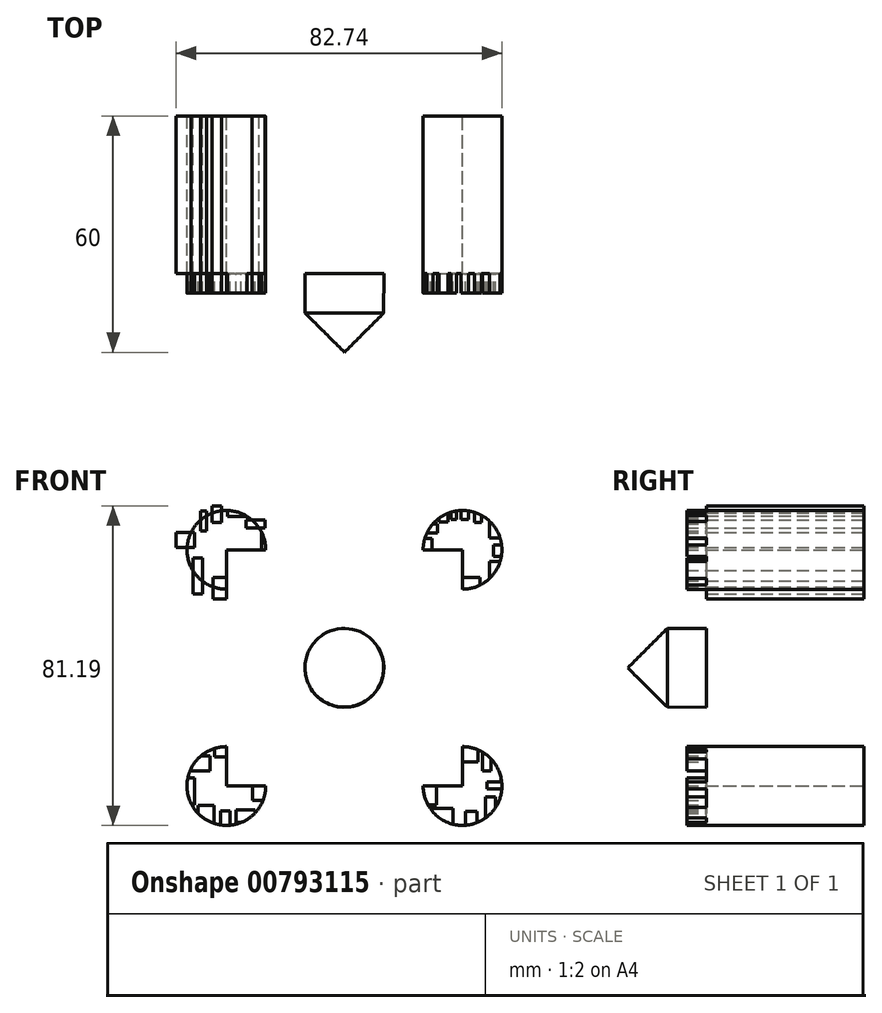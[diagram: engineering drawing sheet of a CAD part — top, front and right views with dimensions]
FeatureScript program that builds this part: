
annotation { "Feature Type Name" : "Feature", "Feature Type Description" : "" }
export const myFeature = defineFeature(function(context is Context, id is Id, definition is map)
    precondition{}
    {
        {
            var Q0;
            Q0=qCreatedBy(makeId("Front.planeOp"),FACE);
            var sketch = newSketch(context, id + "F0", { "sketchPlane" : qUnion([Q0])});
            skLineSegment(sketch, "E0.top", {"start": v(-31.3, 38.66) * mm, "end": v(28.7, 38.66) * mm});
            skLineSegment(sketch, "E0.right", {"start": v(28.7, -21.34) * mm, "end": v(28.7, 38.66) * mm});
            skCircle(sketch, "E1", {"center": v(-31.3, 38.66) * mm, "radius": 10 * mm});
            skCircle(sketch, "E2", {"center": v(28.7, 38.66) * mm, "radius": 10 * mm});
            skCircle(sketch, "E3", {"center": v(-31.3, -21.34) * mm, "radius": 10 * mm});
            skLineSegment(sketch, "E4", {"start": v(28.7, -21.34) * mm, "end": v(-31.3, -21.34) * mm});
            skLineSegment(sketch, "E5", {"start": v(-31.3, 38.66) * mm, "end": v(-31.3, -21.34) * mm});
            skLineSegment(sketch, "E6.bottom", {"start": v(-31.3, 26.14) * mm, "end": v(-34.66, 26.14) * mm});
            skLineSegment(sketch, "E6.top", {"start": v(-31.3, 31.59) * mm, "end": v(-34.66, 31.59) * mm});
            skLineSegment(sketch, "E6.left", {"start": v(-31.3, 26.14) * mm, "end": v(-31.3, 31.59) * mm});
            skLineSegment(sketch, "E6.right", {"start": v(-34.66, 26.14) * mm, "end": v(-34.66, 31.59) * mm});
            skLineSegment(sketch, "E7.bottom", {"start": v(-37.36, 27.46) * mm, "end": v(-39.78, 27.46) * mm});
            skLineSegment(sketch, "E7.top", {"start": v(-37.36, 36.62) * mm, "end": v(-39.78, 36.62) * mm});
            skLineSegment(sketch, "E7.left", {"start": v(-37.36, 27.46) * mm, "end": v(-37.36, 36.62) * mm});
            skLineSegment(sketch, "E7.right", {"start": v(-39.78, 27.46) * mm, "end": v(-39.78, 36.62) * mm});
            skLineSegment(sketch, "E8.bottom", {"start": v(-19.52, 38.66) * mm, "end": v(-22.4, 38.66) * mm});
            skLineSegment(sketch, "E8.top", {"start": v(-19.52, 43.23) * mm, "end": v(-22.4, 43.23) * mm});
            skLineSegment(sketch, "E8.left", {"start": v(-19.52, 38.66) * mm, "end": v(-19.52, 43.23) * mm});
            skLineSegment(sketch, "E8.right", {"start": v(-22.4, 38.66) * mm, "end": v(-22.4, 43.23) * mm});
            skLineSegment(sketch, "E9.bottom", {"start": v(-21.44, 46.19) * mm, "end": v(-26.35, 46.19) * mm});
            skLineSegment(sketch, "E9.top", {"start": v(-21.44, 44.24) * mm, "end": v(-26.35, 44.24) * mm});
            skLineSegment(sketch, "E9.left", {"start": v(-21.44, 46.19) * mm, "end": v(-21.44, 44.24) * mm});
            skLineSegment(sketch, "E9.right", {"start": v(-26.35, 46.19) * mm, "end": v(-26.35, 44.24) * mm});
            skLineSegment(sketch, "E10.bottom", {"start": v(-25.81, 49.08) * mm, "end": v(-30.99, 49.08) * mm});
            skLineSegment(sketch, "E10.top", {"start": v(-25.81, 47.12) * mm, "end": v(-30.99, 47.12) * mm});
            skLineSegment(sketch, "E10.left", {"start": v(-25.81, 49.08) * mm, "end": v(-25.81, 47.12) * mm});
            skLineSegment(sketch, "E10.right", {"start": v(-30.99, 49.08) * mm, "end": v(-30.99, 47.12) * mm});
            skLineSegment(sketch, "E11.bottom", {"start": v(-32.51, 49.85) * mm, "end": v(-34.9, 49.85) * mm});
            skLineSegment(sketch, "E11.top", {"start": v(-32.51, 45.58) * mm, "end": v(-34.9, 45.58) * mm});
            skLineSegment(sketch, "E11.left", {"start": v(-32.51, 49.85) * mm, "end": v(-32.51, 45.58) * mm});
            skLineSegment(sketch, "E11.right", {"start": v(-34.9, 49.85) * mm, "end": v(-34.9, 45.58) * mm});
            skLineSegment(sketch, "E12.bottom", {"start": v(-37.8, 48.54) * mm, "end": v(-36.34, 48.54) * mm});
            skLineSegment(sketch, "E12.top", {"start": v(-37.8, 43.44) * mm, "end": v(-36.34, 43.44) * mm});
            skLineSegment(sketch, "E12.left", {"start": v(-37.8, 48.54) * mm, "end": v(-37.8, 43.44) * mm});
            skLineSegment(sketch, "E12.right", {"start": v(-36.34, 48.54) * mm, "end": v(-36.34, 43.44) * mm});
            skLineSegment(sketch, "E13.bottom", {"start": v(-44.04, 43.08) * mm, "end": v(-39.35, 43.08) * mm});
            skLineSegment(sketch, "E13.top", {"start": v(-44.04, 39.2) * mm, "end": v(-39.35, 39.2) * mm});
            skLineSegment(sketch, "E13.left", {"start": v(-44.04, 43.08) * mm, "end": v(-44.04, 39.2) * mm});
            skLineSegment(sketch, "E13.right", {"start": v(-39.35, 43.08) * mm, "end": v(-39.35, 39.2) * mm});
            skLineSegment(sketch, "E14.bottom", {"start": v(17.29, 38.66) * mm, "end": v(20.94, 38.66) * mm});
            skLineSegment(sketch, "E14.top", {"start": v(17.29, 41.51) * mm, "end": v(20.94, 41.51) * mm});
            skLineSegment(sketch, "E14.left", {"start": v(17.29, 38.66) * mm, "end": v(17.29, 41.51) * mm});
            skLineSegment(sketch, "E14.right", {"start": v(20.94, 38.66) * mm, "end": v(20.94, 41.51) * mm});
            skLineSegment(sketch, "E15.bottom", {"start": v(19, 42.93) * mm, "end": v(22.3, 42.93) * mm});
            skLineSegment(sketch, "E15.top", {"start": v(19, 45.24) * mm, "end": v(22.3, 45.24) * mm});
            skLineSegment(sketch, "E15.left", {"start": v(19, 42.93) * mm, "end": v(19, 45.24) * mm});
            skLineSegment(sketch, "E15.right", {"start": v(22.3, 42.93) * mm, "end": v(22.3, 45.24) * mm});
            skLineSegment(sketch, "E16.bottom", {"start": v(22.73, 48.54) * mm, "end": v(25, 48.54) * mm});
            skLineSegment(sketch, "E16.top", {"start": v(22.73, 45.75) * mm, "end": v(25, 45.75) * mm});
            skLineSegment(sketch, "E16.left", {"start": v(22.73, 48.54) * mm, "end": v(22.73, 45.75) * mm});
            skLineSegment(sketch, "E16.right", {"start": v(25, 48.54) * mm, "end": v(25, 45.75) * mm});
            skLineSegment(sketch, "E17.bottom", {"start": v(27.22, 48.99) * mm, "end": v(25.81, 48.99) * mm});
            skLineSegment(sketch, "E17.top", {"start": v(27.22, 46.33) * mm, "end": v(25.81, 46.33) * mm});
            skLineSegment(sketch, "E17.left", {"start": v(27.22, 48.99) * mm, "end": v(27.22, 46.33) * mm});
            skLineSegment(sketch, "E17.right", {"start": v(25.81, 48.99) * mm, "end": v(25.81, 46.33) * mm});
            skLineSegment(sketch, "E18.bottom", {"start": v(28.32, 49.76) * mm, "end": v(30.22, 49.76) * mm});
            skLineSegment(sketch, "E18.top", {"start": v(28.32, 46.32) * mm, "end": v(30.22, 46.32) * mm});
            skLineSegment(sketch, "E18.left", {"start": v(28.32, 49.76) * mm, "end": v(28.32, 46.32) * mm});
            skLineSegment(sketch, "E18.right", {"start": v(30.22, 49.76) * mm, "end": v(30.22, 46.32) * mm});
            skLineSegment(sketch, "E19.bottom", {"start": v(31.72, 49.12) * mm, "end": v(33.5, 49.12) * mm});
            skLineSegment(sketch, "E19.top", {"start": v(31.72, 45.6) * mm, "end": v(33.5, 45.6) * mm});
            skLineSegment(sketch, "E19.left", {"start": v(31.72, 49.12) * mm, "end": v(31.72, 45.6) * mm});
            skLineSegment(sketch, "E19.right", {"start": v(33.5, 49.12) * mm, "end": v(33.5, 45.6) * mm});
            skCircle(sketch, "E20", {"center": v(28.7, -21.34) * mm, "radius": 10 * mm});
            skLineSegment(sketch, "E21.bottom", {"start": v(28.7, 26.02) * mm, "end": v(33.17, 26.02) * mm});
            skLineSegment(sketch, "E21.top", {"start": v(28.7, 31.7) * mm, "end": v(33.17, 31.7) * mm});
            skLineSegment(sketch, "E21.left", {"start": v(28.7, 26.02) * mm, "end": v(28.7, 31.7) * mm});
            skLineSegment(sketch, "E21.right", {"start": v(33.17, 26.02) * mm, "end": v(33.17, 31.7) * mm});
            skLineSegment(sketch, "E22.bottom", {"start": v(35.6, 29.26) * mm, "end": v(38.26, 29.26) * mm});
            skLineSegment(sketch, "E22.top", {"start": v(35.6, 35.7) * mm, "end": v(38.26, 35.7) * mm});
            skLineSegment(sketch, "E22.left", {"start": v(35.6, 29.26) * mm, "end": v(35.6, 35.7) * mm});
            skLineSegment(sketch, "E22.right", {"start": v(38.26, 29.26) * mm, "end": v(38.26, 35.7) * mm});
            skLineSegment(sketch, "E23.bottom", {"start": v(35.6, 48.4) * mm, "end": v(38.24, 48.4) * mm});
            skLineSegment(sketch, "E23.top", {"start": v(35.6, 41.64) * mm, "end": v(38.24, 41.64) * mm});
            skLineSegment(sketch, "E23.left", {"start": v(35.6, 48.4) * mm, "end": v(35.6, 41.64) * mm});
            skLineSegment(sketch, "E23.right", {"start": v(38.24, 48.4) * mm, "end": v(38.24, 41.64) * mm});
            skLineSegment(sketch, "E24.bottom", {"start": v(40.87, 36.96) * mm, "end": v(36.52, 36.96) * mm});
            skLineSegment(sketch, "E24.top", {"start": v(40.87, 39.9) * mm, "end": v(36.52, 39.9) * mm});
            skLineSegment(sketch, "E24.left", {"start": v(40.87, 36.96) * mm, "end": v(40.87, 39.9) * mm});
            skLineSegment(sketch, "E24.right", {"start": v(36.52, 36.96) * mm, "end": v(36.52, 39.9) * mm});
            skLineSegment(sketch, "E25.bottom", {"start": v(28.7, -8.22) * mm, "end": v(32.65, -8.22) * mm});
            skLineSegment(sketch, "E25.top", {"start": v(28.7, -15.2) * mm, "end": v(32.65, -15.2) * mm});
            skLineSegment(sketch, "E25.left", {"start": v(28.7, -8.22) * mm, "end": v(28.7, -15.2) * mm});
            skLineSegment(sketch, "E25.right", {"start": v(32.65, -8.22) * mm, "end": v(32.65, -15.2) * mm});
            skLineSegment(sketch, "E26.bottom", {"start": v(35.9, -10.63) * mm, "end": v(33.73, -10.63) * mm});
            skLineSegment(sketch, "E26.top", {"start": v(35.9, -17.5) * mm, "end": v(33.73, -17.5) * mm});
            skLineSegment(sketch, "E26.left", {"start": v(35.9, -10.63) * mm, "end": v(35.9, -17.5) * mm});
            skLineSegment(sketch, "E26.right", {"start": v(33.73, -10.63) * mm, "end": v(33.73, -17.5) * mm});
            skLineSegment(sketch, "E27.bottom", {"start": v(15.4, -21.34) * mm, "end": v(22.15, -21.34) * mm});
            skLineSegment(sketch, "E27.top", {"start": v(15.4, -26.11) * mm, "end": v(22.15, -26.11) * mm});
            skLineSegment(sketch, "E27.left", {"start": v(15.4, -21.34) * mm, "end": v(15.4, -26.11) * mm});
            skLineSegment(sketch, "E27.right", {"start": v(22.15, -21.34) * mm, "end": v(22.15, -26.11) * mm});
            skLineSegment(sketch, "E28.bottom", {"start": v(19.62, -31.77) * mm, "end": v(26.25, -31.77) * mm});
            skLineSegment(sketch, "E28.top", {"start": v(19.62, -27.07) * mm, "end": v(26.25, -27.07) * mm});
            skLineSegment(sketch, "E28.left", {"start": v(19.62, -31.77) * mm, "end": v(19.62, -27.07) * mm});
            skLineSegment(sketch, "E28.right", {"start": v(26.25, -31.77) * mm, "end": v(26.25, -27.07) * mm});
            skLineSegment(sketch, "E29.bottom", {"start": v(29.5, -34.42) * mm, "end": v(32.39, -34.42) * mm});
            skLineSegment(sketch, "E29.top", {"start": v(29.5, -27.8) * mm, "end": v(32.39, -27.8) * mm});
            skLineSegment(sketch, "E29.left", {"start": v(29.5, -34.42) * mm, "end": v(29.5, -27.8) * mm});
            skLineSegment(sketch, "E29.right", {"start": v(32.39, -34.42) * mm, "end": v(32.39, -27.8) * mm});
            skLineSegment(sketch, "E30.bottom", {"start": v(37.08, -29.48) * mm, "end": v(34.56, -29.48) * mm});
            skLineSegment(sketch, "E30.top", {"start": v(37.08, -24.06) * mm, "end": v(34.56, -24.06) * mm});
            skLineSegment(sketch, "E30.left", {"start": v(37.08, -29.48) * mm, "end": v(37.08, -24.06) * mm});
            skLineSegment(sketch, "E30.right", {"start": v(34.56, -29.48) * mm, "end": v(34.56, -24.06) * mm});
            skLineSegment(sketch, "E31.bottom", {"start": v(41.06, -20.33) * mm, "end": v(34.92, -20.33) * mm});
            skLineSegment(sketch, "E31.top", {"start": v(41.06, -22.14) * mm, "end": v(34.92, -22.14) * mm});
            skLineSegment(sketch, "E31.left", {"start": v(41.06, -20.33) * mm, "end": v(41.06, -22.14) * mm});
            skLineSegment(sketch, "E31.right", {"start": v(34.92, -20.33) * mm, "end": v(34.92, -22.14) * mm});
            skLineSegment(sketch, "E32.bottom", {"start": v(-18.04, -21.34) * mm, "end": v(-24.67, -21.34) * mm});
            skLineSegment(sketch, "E32.top", {"start": v(-18.04, -24.96) * mm, "end": v(-24.67, -24.96) * mm});
            skLineSegment(sketch, "E32.left", {"start": v(-18.04, -21.34) * mm, "end": v(-18.04, -24.96) * mm});
            skLineSegment(sketch, "E32.right", {"start": v(-24.67, -21.34) * mm, "end": v(-24.67, -24.96) * mm});
            skLineSegment(sketch, "E33.bottom", {"start": v(-24.07, -30.62) * mm, "end": v(-28.88, -30.62) * mm});
            skLineSegment(sketch, "E33.top", {"start": v(-24.07, -27.37) * mm, "end": v(-28.88, -27.37) * mm});
            skLineSegment(sketch, "E33.left", {"start": v(-24.07, -30.62) * mm, "end": v(-24.07, -27.37) * mm});
            skLineSegment(sketch, "E33.right", {"start": v(-28.88, -30.62) * mm, "end": v(-28.88, -27.37) * mm});
            skLineSegment(sketch, "E34.bottom", {"start": v(-32.74, -33.39) * mm, "end": v(-30.33, -33.39) * mm});
            skLineSegment(sketch, "E34.top", {"start": v(-32.74, -27.6) * mm, "end": v(-30.33, -27.6) * mm});
            skLineSegment(sketch, "E34.left", {"start": v(-32.74, -33.39) * mm, "end": v(-32.74, -27.6) * mm});
            skLineSegment(sketch, "E34.right", {"start": v(-30.33, -33.39) * mm, "end": v(-30.33, -27.6) * mm});
            skLineSegment(sketch, "E35.bottom", {"start": v(-38.52, -31.1) * mm, "end": v(-34.42, -31.1) * mm});
            skLineSegment(sketch, "E35.top", {"start": v(-38.52, -26.28) * mm, "end": v(-34.42, -26.28) * mm});
            skLineSegment(sketch, "E35.left", {"start": v(-38.52, -31.1) * mm, "end": v(-38.52, -26.28) * mm});
            skLineSegment(sketch, "E35.right", {"start": v(-34.42, -31.1) * mm, "end": v(-34.42, -26.28) * mm});
            skLineSegment(sketch, "E36.bottom", {"start": v(-42.85, -26.16) * mm, "end": v(-39.36, -26.16) * mm});
            skLineSegment(sketch, "E36.top", {"start": v(-42.85, -19.3) * mm, "end": v(-39.36, -19.3) * mm});
            skLineSegment(sketch, "E36.left", {"start": v(-42.85, -26.16) * mm, "end": v(-42.85, -19.3) * mm});
            skLineSegment(sketch, "E36.right", {"start": v(-39.36, -26.16) * mm, "end": v(-39.36, -19.3) * mm});
            skLineSegment(sketch, "E37.bottom", {"start": v(-41.9, -13.64) * mm, "end": v(-35.39, -13.64) * mm});
            skLineSegment(sketch, "E37.top", {"start": v(-41.9, -17.5) * mm, "end": v(-35.39, -17.5) * mm});
            skLineSegment(sketch, "E37.left", {"start": v(-41.9, -13.64) * mm, "end": v(-41.9, -17.5) * mm});
            skLineSegment(sketch, "E37.right", {"start": v(-35.39, -13.64) * mm, "end": v(-35.39, -17.5) * mm});
            skLineSegment(sketch, "E38.bottom", {"start": v(-31.3, -7.86) * mm, "end": v(-34.3, -7.86) * mm});
            skLineSegment(sketch, "E38.top", {"start": v(-31.3, -14) * mm, "end": v(-34.3, -14) * mm});
            skLineSegment(sketch, "E38.left", {"start": v(-31.3, -7.86) * mm, "end": v(-31.3, -14) * mm});
            skLineSegment(sketch, "E38.right", {"start": v(-34.3, -7.86) * mm, "end": v(-34.3, -14) * mm});
            skSolve(sketch);
        }
        {
            var Q0;
            {var subQ0=sQuery(id+"F0.wireOp",EDGE,"E8.bottom");var subQ3=sQuery(id+"F0.wireOp",EDGE,"E1");var subQ4=makeQuery(id+"F0.imprint","INTERSECT",VERTEX,{"derivedFrom":[subQ3,subQ0]});Q0=makeQuery(id+"F0.imprint","IMPRINT",FACE,{"disambiguationData":[TD([[makeQuery(id+"F0.imprint","IMPRINT",EDGE,{"disambiguationData":[TD([[subQ4,1.0]])],"derivedFrom":subQ3}),-1.0]])]});}
            var Q1;
            {var subQ3=sQuery(id+"F0.wireOp",EDGE,"E3");var subQ7=sQuery(id+"F0.wireOp",EDGE,"E38.left");var subQ9=makeQuery(id+"F0.imprint","INTERSECT",VERTEX,{"derivedFrom":[subQ3,subQ7]});Q1=makeQuery(id+"F0.imprint","IMPRINT",FACE,{"disambiguationData":[TD([[makeQuery(id+"F0.imprint","IMPRINT",EDGE,{"disambiguationData":[TD([[subQ9,1.0]])],"derivedFrom":subQ3}),1.0]])]});}
            var Q2;
            {var subQ0=sQuery(id+"F0.wireOp",EDGE,"E25.left");var subQ3=sQuery(id+"F0.wireOp",EDGE,"E20");var subQ4=makeQuery(id+"F0.imprint","INTERSECT",VERTEX,{"derivedFrom":[subQ3,subQ0]});Q2=makeQuery(id+"F0.imprint","IMPRINT",FACE,{"disambiguationData":[TD([[makeQuery(id+"F0.imprint","IMPRINT",EDGE,{"disambiguationData":[TD([[subQ4,-1.0]])],"derivedFrom":subQ3}),1.0]])]});}
            var Q3;
            {var subQ0=sQuery(id+"F0.wireOp",EDGE,"E14.bottom");var subQ1=sQuery(id+"F0.wireOp",EDGE,"E2");var subQ2=makeQuery(id+"F0.imprint","INTERSECT",VERTEX,{"derivedFrom":[subQ1,subQ0]});Q3=makeQuery(id+"F0.imprint","IMPRINT",FACE,{"disambiguationData":[TD([[makeQuery(id+"F0.imprint","IMPRINT",EDGE,{"disambiguationData":[TD([[subQ2,-1.0]])],"derivedFrom":subQ1}),1.0]])]});}
            var Q4;
            {var subQ5=sQuery(id+"F0.wireOp",EDGE,"E8.bottom");var subQ6=sQuery(id+"F0.wireOp",EDGE,"E1");var subQ7=makeQuery(id+"F0.imprint","INTERSECT",VERTEX,{"derivedFrom":[subQ6,subQ5]});Q4=makeQuery(id+"F0.imprint","IMPRINT",FACE,{"disambiguationData":[TD([[makeQuery(id+"F0.imprint","IMPRINT",EDGE,{"disambiguationData":[TD([[subQ7,1.0]])],"derivedFrom":subQ6}),1.0]])]});}
            var Q5;
            {var subQ19=sQuery(id+"F0.wireOp",EDGE,"E6.top");Q5=makeQuery(id+"F0.imprint","IMPRINT",FACE,{"disambiguationData":[TD([[makeQuery(id+"F0.imprint","IMPRINT",EDGE,{"derivedFrom":subQ19}),-1.0]])]});}
            var Q6;
            {var subQ6=sQuery(id+"F0.wireOp",EDGE,"E14.right");Q6=makeQuery(id+"F0.imprint","IMPRINT",FACE,{"disambiguationData":[TD([[makeQuery(id+"F0.imprint","IMPRINT",EDGE,{"derivedFrom":subQ6}),-1.0]])]});}
            var Q7;
            {var subQ12=sQuery(id+"F0.wireOp",EDGE,"E32.right");Q7=makeQuery(id+"F0.imprint","IMPRINT",FACE,{"disambiguationData":[TD([[makeQuery(id+"F0.imprint","IMPRINT",EDGE,{"derivedFrom":subQ12}),-1.0]])]});}
            var Q8;
            {var subQ33=sQuery(id+"F0.wireOp",EDGE,"E25.top");Q8=makeQuery(id+"F0.imprint","IMPRINT",FACE,{"disambiguationData":[TD([[makeQuery(id+"F0.imprint","IMPRINT",EDGE,{"derivedFrom":subQ33}),-1.0]])]});}
            extrude(context, id + "F1", {"entities" : qUnion([Q0, Q1, Q2, Q3, Q4, Q5, Q6, Q7, Q8]), "depth" : 40 * mm, "offsetDistance" : 25 * mm});
        }
        {
            var Q0;
            {var subQ0=sQuery(id+"F0.wireOp",EDGE,"E8.right");Q0=makeQuery(id+"F0.imprint","IMPRINT",FACE,{"disambiguationData":[TD([[makeQuery(id+"F0.imprint","IMPRINT",EDGE,{"derivedFrom":subQ0}),-1.0]])]});}
            var Q1;
            {var subQ5=sQuery(id+"F0.wireOp",EDGE,"E9.right");Q1=makeQuery(id+"F0.imprint","IMPRINT",FACE,{"disambiguationData":[TD([[makeQuery(id+"F0.imprint","IMPRINT",EDGE,{"derivedFrom":subQ5}),1.0]])]});}
            var Q2;
            {var subQ0=sQuery(id+"F0.wireOp",EDGE,"E10.top");var subQ1=sQuery(id+"F0.wireOp",EDGE,"E1");var subQ2=makeQuery(id+"F0.imprint","INTERSECT",VERTEX,{"derivedFrom":[subQ1,subQ0]});Q2=makeQuery(id+"F0.imprint","IMPRINT",FACE,{"disambiguationData":[TD([[makeQuery(id+"F0.imprint","IMPRINT",EDGE,{"disambiguationData":[TD([[subQ2,-1.0]])],"derivedFrom":subQ1}),1.0]])]});}
            var Q3;
            {var subQ5=sQuery(id+"F0.wireOp",EDGE,"E11.top");Q3=makeQuery(id+"F0.imprint","IMPRINT",FACE,{"disambiguationData":[TD([[makeQuery(id+"F0.imprint","IMPRINT",EDGE,{"derivedFrom":subQ5}),-1.0]])]});}
            var Q4;
            {var subQ5=sQuery(id+"F0.wireOp",EDGE,"E12.top");Q4=makeQuery(id+"F0.imprint","IMPRINT",FACE,{"disambiguationData":[TD([[makeQuery(id+"F0.imprint","IMPRINT",EDGE,{"derivedFrom":subQ5}),1.0]])]});}
            var Q5;
            {var subQ5=sQuery(id+"F0.wireOp",EDGE,"E13.right");Q5=makeQuery(id+"F0.imprint","IMPRINT",FACE,{"disambiguationData":[TD([[makeQuery(id+"F0.imprint","IMPRINT",EDGE,{"derivedFrom":subQ5}),-1.0]])]});}
            var Q6;
            {var subQ5=sQuery(id+"F0.wireOp",EDGE,"E7.top");Q6=makeQuery(id+"F0.imprint","IMPRINT",FACE,{"disambiguationData":[TD([[makeQuery(id+"F0.imprint","IMPRINT",EDGE,{"derivedFrom":subQ5}),1.0]])]});}
            var Q7;
            {var subQ5=sQuery(id+"F0.wireOp",EDGE,"E6.top");Q7=makeQuery(id+"F0.imprint","IMPRINT",FACE,{"disambiguationData":[TD([[makeQuery(id+"F0.imprint","IMPRINT",EDGE,{"derivedFrom":subQ5}),1.0]])]});}
            var Q8;
            {var subQ5=sQuery(id+"F0.wireOp",EDGE,"E38.top");Q8=makeQuery(id+"F0.imprint","IMPRINT",FACE,{"disambiguationData":[TD([[makeQuery(id+"F0.imprint","IMPRINT",EDGE,{"derivedFrom":subQ5}),-1.0]])]});}
            var Q9;
            {var subQ5=sQuery(id+"F0.wireOp",EDGE,"E37.right");Q9=makeQuery(id+"F0.imprint","IMPRINT",FACE,{"disambiguationData":[TD([[makeQuery(id+"F0.imprint","IMPRINT",EDGE,{"derivedFrom":subQ5}),-1.0]])]});}
            var Q10;
            {var subQ5=sQuery(id+"F0.wireOp",EDGE,"E36.right");Q10=makeQuery(id+"F0.imprint","IMPRINT",FACE,{"disambiguationData":[TD([[makeQuery(id+"F0.imprint","IMPRINT",EDGE,{"derivedFrom":subQ5}),1.0]])]});}
            var Q11;
            {var subQ5=sQuery(id+"F0.wireOp",EDGE,"E35.top");Q11=makeQuery(id+"F0.imprint","IMPRINT",FACE,{"disambiguationData":[TD([[makeQuery(id+"F0.imprint","IMPRINT",EDGE,{"derivedFrom":subQ5}),-1.0]])]});}
            var Q12;
            {var subQ5=sQuery(id+"F0.wireOp",EDGE,"E34.top");Q12=makeQuery(id+"F0.imprint","IMPRINT",FACE,{"disambiguationData":[TD([[makeQuery(id+"F0.imprint","IMPRINT",EDGE,{"derivedFrom":subQ5}),-1.0]])]});}
            var Q13;
            {var subQ0=sQuery(id+"F0.wireOp",EDGE,"E33.top");Q13=makeQuery(id+"F0.imprint","IMPRINT",FACE,{"disambiguationData":[TD([[makeQuery(id+"F0.imprint","IMPRINT",EDGE,{"derivedFrom":subQ0}),1.0]])]});}
            var Q14;
            {var subQ5=sQuery(id+"F0.wireOp",EDGE,"E32.right");Q14=makeQuery(id+"F0.imprint","IMPRINT",FACE,{"disambiguationData":[TD([[makeQuery(id+"F0.imprint","IMPRINT",EDGE,{"derivedFrom":subQ5}),1.0]])]});}
            var Q15;
            {var subQ5=sQuery(id+"F0.wireOp",EDGE,"E27.right");Q15=makeQuery(id+"F0.imprint","IMPRINT",FACE,{"disambiguationData":[TD([[makeQuery(id+"F0.imprint","IMPRINT",EDGE,{"derivedFrom":subQ5}),-1.0]])]});}
            var Q16;
            {var subQ0=sQuery(id+"F0.wireOp",EDGE,"E28.top");var subQ1=sQuery(id+"F0.wireOp",EDGE,"E20");var subQ2=makeQuery(id+"F0.imprint","INTERSECT",VERTEX,{"derivedFrom":[subQ1,subQ0]});Q16=makeQuery(id+"F0.imprint","IMPRINT",FACE,{"disambiguationData":[TD([[makeQuery(id+"F0.imprint","IMPRINT",EDGE,{"disambiguationData":[TD([[subQ2,-1.0]])],"derivedFrom":subQ1}),1.0]])]});}
            var Q17;
            {var subQ5=sQuery(id+"F0.wireOp",EDGE,"E29.top");Q17=makeQuery(id+"F0.imprint","IMPRINT",FACE,{"disambiguationData":[TD([[makeQuery(id+"F0.imprint","IMPRINT",EDGE,{"derivedFrom":subQ5}),-1.0]])]});}
            var Q18;
            {var subQ5=sQuery(id+"F0.wireOp",EDGE,"E30.top");Q18=makeQuery(id+"F0.imprint","IMPRINT",FACE,{"disambiguationData":[TD([[makeQuery(id+"F0.imprint","IMPRINT",EDGE,{"derivedFrom":subQ5}),1.0]])]});}
            var Q19;
            {var subQ5=sQuery(id+"F0.wireOp",EDGE,"E31.right");Q19=makeQuery(id+"F0.imprint","IMPRINT",FACE,{"disambiguationData":[TD([[makeQuery(id+"F0.imprint","IMPRINT",EDGE,{"derivedFrom":subQ5}),1.0]])]});}
            var Q20;
            {var subQ5=sQuery(id+"F0.wireOp",EDGE,"E26.top");Q20=makeQuery(id+"F0.imprint","IMPRINT",FACE,{"disambiguationData":[TD([[makeQuery(id+"F0.imprint","IMPRINT",EDGE,{"derivedFrom":subQ5}),-1.0]])]});}
            var Q21;
            {var subQ5=sQuery(id+"F0.wireOp",EDGE,"E25.top");Q21=makeQuery(id+"F0.imprint","IMPRINT",FACE,{"disambiguationData":[TD([[makeQuery(id+"F0.imprint","IMPRINT",EDGE,{"derivedFrom":subQ5}),1.0]])]});}
            var Q22;
            {var subQ5=sQuery(id+"F0.wireOp",EDGE,"E14.right");Q22=makeQuery(id+"F0.imprint","IMPRINT",FACE,{"disambiguationData":[TD([[makeQuery(id+"F0.imprint","IMPRINT",EDGE,{"derivedFrom":subQ5}),1.0]])]});}
            var Q23;
            {var subQ5=sQuery(id+"F0.wireOp",EDGE,"E16.top");Q23=makeQuery(id+"F0.imprint","IMPRINT",FACE,{"disambiguationData":[TD([[makeQuery(id+"F0.imprint","IMPRINT",EDGE,{"derivedFrom":subQ5}),1.0]])]});}
            var Q24;
            {var subQ5=sQuery(id+"F0.wireOp",EDGE,"E17.top");Q24=makeQuery(id+"F0.imprint","IMPRINT",FACE,{"disambiguationData":[TD([[makeQuery(id+"F0.imprint","IMPRINT",EDGE,{"derivedFrom":subQ5}),-1.0]])]});}
            var Q25;
            {var subQ5=sQuery(id+"F0.wireOp",EDGE,"E18.top");Q25=makeQuery(id+"F0.imprint","IMPRINT",FACE,{"disambiguationData":[TD([[makeQuery(id+"F0.imprint","IMPRINT",EDGE,{"derivedFrom":subQ5}),1.0]])]});}
            var Q26;
            {var subQ5=sQuery(id+"F0.wireOp",EDGE,"E19.top");Q26=makeQuery(id+"F0.imprint","IMPRINT",FACE,{"disambiguationData":[TD([[makeQuery(id+"F0.imprint","IMPRINT",EDGE,{"derivedFrom":subQ5}),1.0]])]});}
            var Q27;
            {var subQ0=sQuery(id+"F0.wireOp",EDGE,"E23.top");Q27=makeQuery(id+"F0.imprint","IMPRINT",FACE,{"disambiguationData":[TD([[makeQuery(id+"F0.imprint","IMPRINT",EDGE,{"derivedFrom":subQ0}),1.0]])]});}
            var Q28;
            {var subQ5=sQuery(id+"F0.wireOp",EDGE,"E24.right");Q28=makeQuery(id+"F0.imprint","IMPRINT",FACE,{"disambiguationData":[TD([[makeQuery(id+"F0.imprint","IMPRINT",EDGE,{"derivedFrom":subQ5}),-1.0]])]});}
            var Q29;
            {var subQ0=sQuery(id+"F0.wireOp",EDGE,"E22.top");Q29=makeQuery(id+"F0.imprint","IMPRINT",FACE,{"disambiguationData":[TD([[makeQuery(id+"F0.imprint","IMPRINT",EDGE,{"derivedFrom":subQ0}),-1.0]])]});}
            var Q30;
            {var subQ5=sQuery(id+"F0.wireOp",EDGE,"E21.top");Q30=makeQuery(id+"F0.imprint","IMPRINT",FACE,{"disambiguationData":[TD([[makeQuery(id+"F0.imprint","IMPRINT",EDGE,{"derivedFrom":subQ5}),-1.0]])]});}
            var Q31;
            {var subQ5=sQuery(id+"F0.wireOp",EDGE,"E15.right");Q31=makeQuery(id+"F0.imprint","IMPRINT",FACE,{"disambiguationData":[TD([[makeQuery(id+"F0.imprint","IMPRINT",EDGE,{"derivedFrom":subQ5}),1.0]])]});}
            extrude(context, id + "F2", {"entities" : qUnion([Q0, Q1, Q2, Q3, Q4, Q5, Q6, Q7, Q8, Q9, Q10, Q11, Q12, Q13, Q14, Q15, Q16, Q17, Q18, Q19, Q20, Q21, Q22, Q23, Q24, Q25, Q26, Q27, Q28, Q29, Q30, Q31]), "operationType" : NewBodyOperationType.ADD, "depth" : 45 * mm, "offsetDistance" : 25 * mm});
        }
        {
            var Q0;
            Q0=makeQuery(id+"F1.opExtrude","CAP_FACE",FACE,{"disambiguationData":[OSD([sQuery(id+"F0.wireOp",EDGE,"E0.top"),sQuery(id+"F0.wireOp",EDGE,"E0.right"),sQuery(id+"F0.wireOp",EDGE,"E1"),sQuery(id+"F0.wireOp",EDGE,"E2"),sQuery(id+"F0.wireOp",EDGE,"E3"),sQuery(id+"F0.wireOp",EDGE,"E4"),sQuery(id+"F0.wireOp",EDGE,"E5"),sQuery(id+"F0.wireOp",EDGE,"E6.top"),sQuery(id+"F0.wireOp",EDGE,"E6.left"),sQuery(id+"F0.wireOp",EDGE,"E6.right"),sQuery(id+"F0.wireOp",EDGE,"E7.top"),sQuery(id+"F0.wireOp",EDGE,"E7.left"),sQuery(id+"F0.wireOp",EDGE,"E7.right"),sQuery(id+"F0.wireOp",EDGE,"E8.bottom"),sQuery(id+"F0.wireOp",EDGE,"E8.right"),sQuery(id+"F0.wireOp",EDGE,"E9.bottom"),sQuery(id+"F0.wireOp",EDGE,"E9.top"),sQuery(id+"F0.wireOp",EDGE,"E9.right"),sQuery(id+"F0.wireOp",EDGE,"E10.top"),sQuery(id+"F0.wireOp",EDGE,"E10.right"),sQuery(id+"F0.wireOp",EDGE,"E11.top"),sQuery(id+"F0.wireOp",EDGE,"E11.left"),sQuery(id+"F0.wireOp",EDGE,"E11.right"),sQuery(id+"F0.wireOp",EDGE,"E12.top"),sQuery(id+"F0.wireOp",EDGE,"E12.left"),sQuery(id+"F0.wireOp",EDGE,"E12.right"),sQuery(id+"F0.wireOp",EDGE,"E13.bottom"),sQuery(id+"F0.wireOp",EDGE,"E13.top"),sQuery(id+"F0.wireOp",EDGE,"E13.right"),sQuery(id+"F0.wireOp",EDGE,"E14.bottom"),sQuery(id+"F0.wireOp",EDGE,"E14.top"),sQuery(id+"F0.wireOp",EDGE,"E14.right"),sQuery(id+"F0.wireOp",EDGE,"E15.bottom"),sQuery(id+"F0.wireOp",EDGE,"E15.top"),sQuery(id+"F0.wireOp",EDGE,"E15.right"),sQuery(id+"F0.wireOp",EDGE,"E16.top"),sQuery(id+"F0.wireOp",EDGE,"E16.left"),sQuery(id+"F0.wireOp",EDGE,"E16.right"),sQuery(id+"F0.wireOp",EDGE,"E17.top"),sQuery(id+"F0.wireOp",EDGE,"E17.left"),sQuery(id+"F0.wireOp",EDGE,"E17.right"),sQuery(id+"F0.wireOp",EDGE,"E18.top"),sQuery(id+"F0.wireOp",EDGE,"E18.left"),sQuery(id+"F0.wireOp",EDGE,"E18.right"),sQuery(id+"F0.wireOp",EDGE,"E19.top"),sQuery(id+"F0.wireOp",EDGE,"E19.left"),sQuery(id+"F0.wireOp",EDGE,"E19.right"),sQuery(id+"F0.wireOp",EDGE,"E20"),sQuery(id+"F0.wireOp",EDGE,"E21.top"),sQuery(id+"F0.wireOp",EDGE,"E21.left"),sQuery(id+"F0.wireOp",EDGE,"E21.right"),sQuery(id+"F0.wireOp",EDGE,"E22.top"),sQuery(id+"F0.wireOp",EDGE,"E22.left"),sQuery(id+"F0.wireOp",EDGE,"E23.top"),sQuery(id+"F0.wireOp",EDGE,"E23.left"),sQuery(id+"F0.wireOp",EDGE,"E24.bottom"),sQuery(id+"F0.wireOp",EDGE,"E24.top"),sQuery(id+"F0.wireOp",EDGE,"E24.right"),sQuery(id+"F0.wireOp",EDGE,"E25.top"),sQuery(id+"F0.wireOp",EDGE,"E25.left"),sQuery(id+"F0.wireOp",EDGE,"E25.right"),sQuery(id+"F0.wireOp",EDGE,"E26.top"),sQuery(id+"F0.wireOp",EDGE,"E26.left"),sQuery(id+"F0.wireOp",EDGE,"E26.right"),sQuery(id+"F0.wireOp",EDGE,"E27.bottom"),sQuery(id+"F0.wireOp",EDGE,"E27.top"),sQuery(id+"F0.wireOp",EDGE,"E27.right"),sQuery(id+"F0.wireOp",EDGE,"E28.top"),sQuery(id+"F0.wireOp",EDGE,"E28.right"),sQuery(id+"F0.wireOp",EDGE,"E29.top"),sQuery(id+"F0.wireOp",EDGE,"E29.left"),sQuery(id+"F0.wireOp",EDGE,"E29.right"),sQuery(id+"F0.wireOp",EDGE,"E30.top"),sQuery(id+"F0.wireOp",EDGE,"E30.left"),sQuery(id+"F0.wireOp",EDGE,"E30.right"),sQuery(id+"F0.wireOp",EDGE,"E31.bottom"),sQuery(id+"F0.wireOp",EDGE,"E31.top"),sQuery(id+"F0.wireOp",EDGE,"E31.right"),sQuery(id+"F0.wireOp",EDGE,"E32.bottom"),sQuery(id+"F0.wireOp",EDGE,"E32.top"),sQuery(id+"F0.wireOp",EDGE,"E32.right"),sQuery(id+"F0.wireOp",EDGE,"E33.bottom"),sQuery(id+"F0.wireOp",EDGE,"E33.top"),sQuery(id+"F0.wireOp",EDGE,"E33.left"),sQuery(id+"F0.wireOp",EDGE,"E33.right"),sQuery(id+"F0.wireOp",EDGE,"E34.top"),sQuery(id+"F0.wireOp",EDGE,"E34.left"),sQuery(id+"F0.wireOp",EDGE,"E34.right"),sQuery(id+"F0.wireOp",EDGE,"E35.top"),sQuery(id+"F0.wireOp",EDGE,"E35.left"),sQuery(id+"F0.wireOp",EDGE,"E35.right"),sQuery(id+"F0.wireOp",EDGE,"E36.bottom"),sQuery(id+"F0.wireOp",EDGE,"E36.top"),sQuery(id+"F0.wireOp",EDGE,"E36.right"),sQuery(id+"F0.wireOp",EDGE,"E37.bottom"),sQuery(id+"F0.wireOp",EDGE,"E37.top"),sQuery(id+"F0.wireOp",EDGE,"E37.right"),sQuery(id+"F0.wireOp",EDGE,"E38.top"),sQuery(id+"F0.wireOp",EDGE,"E38.left"),sQuery(id+"F0.wireOp",EDGE,"E38.right")])],"isStart":false});
            var sketch = newSketch(context, id + "F3", { "sketchPlane" : qUnion([Q0])});
            skCircle(sketch, "E39", {"center": v(-1.3, 8.66) * mm, "radius": 10 * mm});
            skPoint(sketch, "E39.centerSnap0", {"position": v(-1.3, 38.66) * mm});
            skPoint(sketch, "E39.centerSnap1", {"position": v(-31.3, 8.66) * mm});
            skSolve(sketch);
        }
        {
            var Q0;
            Q0=qCreatedBy(makeId("Front.planeOp"),FACE);
            cPlane(context, id + "F4", {"entities" : qUnion([Q0]), "cplaneType" : CPlaneType.OFFSET, "offset" : 60 * mm, "width" : 150 * mm, "height" : 150 * mm});
        }
        {
            var Q0;
            Q0=qCreatedBy(id+"F4.planeOp",FACE);
            var sketch = newSketch(context, id + "F5", { "sketchPlane" : qUnion([Q0])});
            skPoint(sketch, "E40", {"position": v(-1.28, 8.67) * mm});
            skSolve(sketch);
        }
        {
            var Q0;
            Q0=qCreatedBy(makeId("Front.planeOp"),FACE);
            cPlane(context, id + "F6", {"entities" : qUnion([Q0]), "cplaneType" : CPlaneType.OFFSET, "offset" : 50 * mm, "width" : 150 * mm, "height" : 150 * mm});
        }
        {
            var Q0;
            Q0=qCreatedBy(id+"F6.planeOp",FACE);
            var sketch = newSketch(context, id + "F7", { "sketchPlane" : qUnion([Q0])});
            skCircle(sketch, "E41", {"center": v(-1.32, 8.7) * mm, "radius": 10 * mm});
            skSolve(sketch);
        }
        {
            var Q1;
            Q1=makeQuery(id+"F3.imprint","IMPRINT",FACE,{"disambiguationData":[TD([[makeQuery(id+"F3.imprint","IMPRINT",EDGE,{"derivedFrom":sQuery(id+"F3.wireOp",EDGE,"E39")}),1.0]])]});
            var Q2;
            Q2=makeQuery(id+"F7.imprint","IMPRINT",FACE,{"disambiguationData":[TD([[makeQuery(id+"F7.imprint","IMPRINT",EDGE,{"derivedFrom":sQuery(id+"F7.wireOp",EDGE,"E41")}),1.0]])]});
            loft(context, id + "F8", {"operationType" : NewBodyOperationType.ADD, "sheetProfilesArray" : [{ "sheetProfileEntities" : qUnion([Q1]) }, { "sheetProfileEntities" : qUnion([Q2]) }]});
        }
        {
            var Q1;
            Q1=makeQuery(id+"F8.opLoft","CAP_FACE",FACE,{"disambiguationData":[OSD([makeQuery(id+"F7.imprint","IMPRINT",FACE,{"disambiguationData":[TD([[makeQuery(id+"F7.imprint","IMPRINT",EDGE,{"derivedFrom":sQuery(id+"F7.wireOp",EDGE,"E41")}),1.0]])]})])],"isStart":true});
            var Q2;
            Q2=sQuery(id+"F5.wireOp",VERTEX,"E40");
            loft(context, id + "F9", {"operationType" : NewBodyOperationType.ADD, "sheetProfilesArray" : [{ "sheetProfileEntities" : qUnion([Q1]) }, { "sheetProfileEntities" : qUnion([Q2]) }]});
        }
    });
